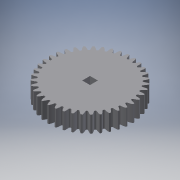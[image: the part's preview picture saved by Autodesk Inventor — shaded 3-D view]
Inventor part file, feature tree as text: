
AUTODESK INVENTOR PART (.ipt)
format: ipt  version: 2017 (Build 210142000, 142)  size: 278,016 bytes
history: native  units: mm
features: extrude x3, sketch x2, pattern_circular x1
ambient origin geometry x8: Origin, YZ Plane, XZ Plane, XY Plane, X Axis, Y Axis, Z Axis, Center Point
bodies: Solid1 (feature_tree)
feature tree (6):
  sketch  "Sketch1"  dims[d0=20.0mm d1=0.0mm]
  extrude  "Extrusion1"  TaperAngle=0.0deg  [1 undecoded]
  extrude  "Extrusion2"  Depth=9.525mm TaperAngle=360.0deg
  pattern_circular  "Circular Pattern1"  [2 undecoded]
  extrude  "Extrusion3"  Depth=9.525mm TaperAngle=0.0deg
  sketch  "Sketch2"  dims[d2=10.0mm d3=0.0mm d4=390.0mm d5=360.0deg d7=9.525mm d8=10.0mm d9=0.0mm]
note: 3 required parameter values undecoded (feature->parameter linkage not recoverable at this tier; creation-order binding heuristic only, values carry confidence <= 0.55)
